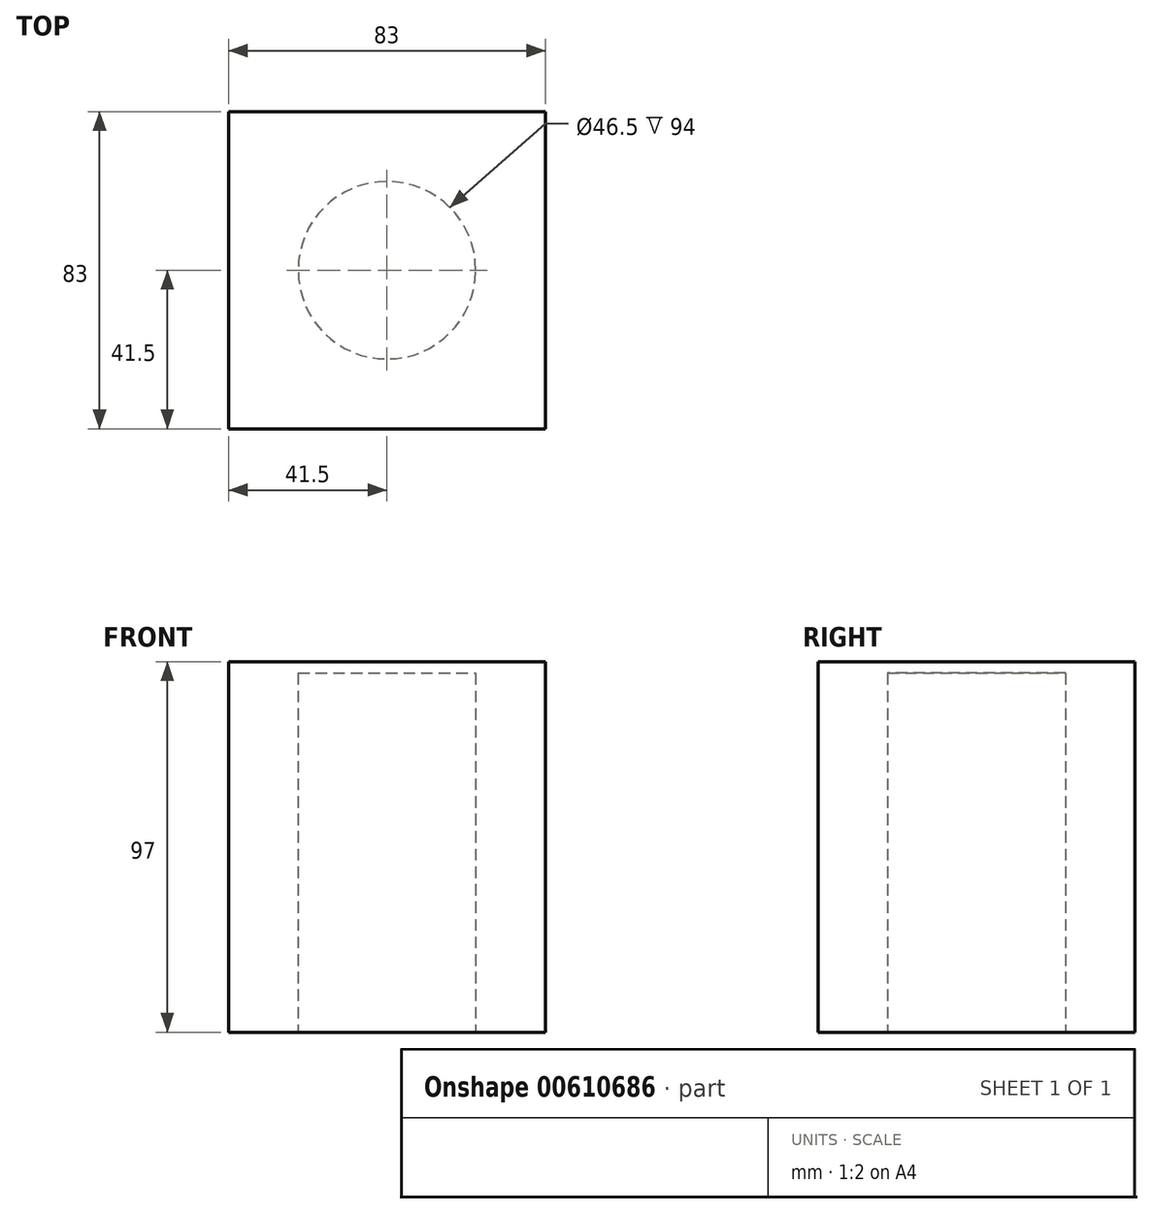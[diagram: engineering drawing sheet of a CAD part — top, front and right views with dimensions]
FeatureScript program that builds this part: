
annotation { "Feature Type Name" : "Feature", "Feature Type Description" : "" }
export const myFeature = defineFeature(function(context is Context, id is Id, definition is map)
    precondition{}
    {
        {
            var Q0;
            Q0=qCreatedBy(makeId("Top.planeOp"),FACE);
            var sketch = newSketch(context, id + "F0", { "sketchPlane" : qUnion([Q0])});
            skLineSegment(sketch, "E0.bottom", {"start": v(41.5, -41.5) * mm, "end": v(-41.5, -41.5) * mm});
            skLineSegment(sketch, "E0.top", {"start": v(41.5, 41.5) * mm, "end": v(-41.5, 41.5) * mm});
            skLineSegment(sketch, "E0.left", {"start": v(41.5, -41.5) * mm, "end": v(41.5, 41.5) * mm});
            skLineSegment(sketch, "E0.right", {"start": v(-41.5, -41.5) * mm, "end": v(-41.5, 41.5) * mm});
            skPoint(sketch, "E0.middle", {"position": v(0, 0) * mm});
            skSolve(sketch);
        }
        {
            var Q0;
            Q0 = qSketchRegion(id + "F0", true);
            extrude(context, id + "F1", {"entities" : qUnion([Q0]), "depth" : 97 * mm, "offsetDistance" : 25 * mm});
        }
        {
            var Q0;
            Q0=makeQuery(id+"F1.opExtrude","CAP_FACE",FACE,{"disambiguationData":[OSD([sQuery(id+"F0.wireOp",EDGE,"E0.bottom"),sQuery(id+"F0.wireOp",EDGE,"E0.top"),sQuery(id+"F0.wireOp",EDGE,"E0.left"),sQuery(id+"F0.wireOp",EDGE,"E0.right")])],"isStart":true});
            var sketch = newSketch(context, id + "F2", { "sketchPlane" : qUnion([Q0])});
            skCircle(sketch, "E1", {"center": v(0, 0) * mm, "radius": 23.25 * mm});
            skSolve(sketch);
        }
        {
            var Q0;
            Q0 = qSketchRegion(id + "F2", true);
            extrude(context, id + "F3", {"entities" : qUnion([Q0]), "operationType" : NewBodyOperationType.REMOVE, "oppositeDirection" : true, "depth" : 94 * mm, "offsetDistance" : 25 * mm});
        }
    });
